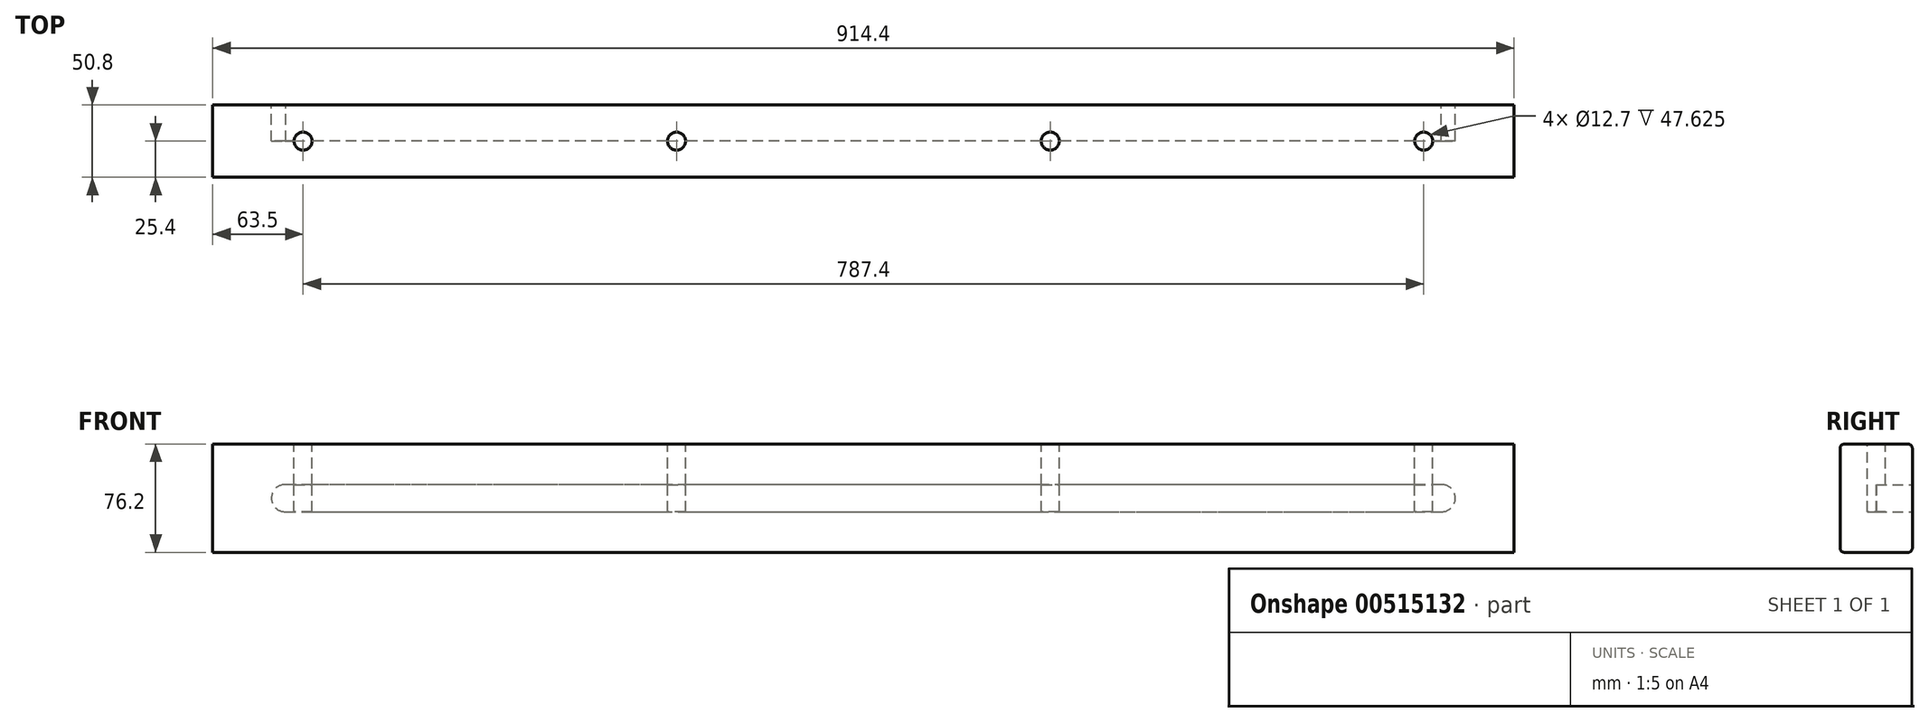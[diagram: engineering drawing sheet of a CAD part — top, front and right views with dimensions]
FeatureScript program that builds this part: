
annotation { "Feature Type Name" : "Feature", "Feature Type Description" : "" }
export const myFeature = defineFeature(function(context is Context, id is Id, definition is map)
    precondition{}
    {
        {
            var Q0;
            Q0=qCreatedBy(makeId("Front.planeOp"),FACE);
            var sketch = newSketch(context, id + "F0", { "sketchPlane" : qUnion([Q0])});
            skLineSegment(sketch, "E0.bottom", {"start": v(-457.2, 38.1) * mm, "end": v(457.2, 38.1) * mm});
            skLineSegment(sketch, "E0.top", {"start": v(-457.2, -38.1) * mm, "end": v(457.2, -38.1) * mm});
            skLineSegment(sketch, "E0.left", {"start": v(-457.2, 38.1) * mm, "end": v(-457.2, -38.1) * mm});
            skLineSegment(sketch, "E0.right", {"start": v(457.2, 38.1) * mm, "end": v(457.2, -38.1) * mm});
            skPoint(sketch, "E0.middle", {"position": v(0, 0) * mm});
            skSolve(sketch);
        }
        {
            var Q0;
            Q0 = qSketchRegion(id + "F0", true);
            extrude(context, id + "F1", {"entities" : qUnion([Q0]), "depth" : 50.8 * mm, "offsetDistance" : 25.4 * mm});
        }
        {
            var Q0;
            Q0=makeQuery(id+"F1.opExtrude","SWEPT_FACE",FACE,{"disambiguationData":[OSD([sQuery(id+"F0.wireOp",EDGE,"E0.bottom")])]});
            var sketch = newSketch(context, id + "F2", { "sketchPlane" : qUnion([Q0])});
            skLineSegment(sketch, "E1", {"start": v(-457.2, -25.4) * mm, "end": v(457.2, -25.4) * mm, "construction": true});
            skCircle(sketch, "E2", {"center": v(-393.7, -25.4) * mm, "radius": 6.35 * mm});
            skCircle(sketch, "E3", {"center": v(393.7, -25.4) * mm, "radius": 6.35 * mm});
            skCircle(sketch, "E4", {"center": v(-131.32, -25.4) * mm, "radius": 6.35 * mm});
            skCircle(sketch, "E5", {"center": v(131.32, -25.4) * mm, "radius": 6.35 * mm});
            skSolve(sketch);
        }
        {
            var Q0;
            Q0 = qSketchRegion(id + "F2", true);
            extrude(context, id + "F3", {"entities" : qUnion([Q0]), "operationType" : NewBodyOperationType.REMOVE, "oppositeDirection" : true, "depth" : 47.62 * mm, "offsetDistance" : 25.4 * mm});
        }
        {
            var Q0;
            Q0=makeQuery(id+"F1.opExtrude","CAP_FACE",FACE,{"disambiguationData":[OSD([sQuery(id+"F0.wireOp",EDGE,"E0.bottom"),sQuery(id+"F0.wireOp",EDGE,"E0.top"),sQuery(id+"F0.wireOp",EDGE,"E0.left"),sQuery(id+"F0.wireOp",EDGE,"E0.right")])],"isStart":true});
            var sketch = newSketch(context, id + "F4", { "sketchPlane" : qUnion([Q0])});
            skArc(sketch, "E6", {"start": v(-406.4, 9.53) * mm, "mid": v(-415.92, -0.23) * mm, "end": v(-405.93, -9.51) * mm});
            skLineSegment(sketch, "E7", {"start": v(-406.4, 9.53) * mm, "end": v(405.93, 9.52) * mm});
            skLineSegment(sketch, "E8", {"start": v(406.4, -9.51) * mm, "end": v(-405.93, -9.51) * mm});
            skArc(sketch, "E9", {"start": v(406.4, -9.51) * mm, "mid": v(415.92, 0.25) * mm, "end": v(405.93, 9.52) * mm});
            skSolve(sketch);
        }
        {
            var Q0;
            Q0 = qSketchRegion(id + "F4", true);
            extrude(context, id + "F5", {"entities" : qUnion([Q0]), "operationType" : NewBodyOperationType.REMOVE, "oppositeDirection" : true, "depth" : 25.4 * mm, "offsetDistance" : 25.4 * mm});
        }
        {
            var Q0;
            Q0=makeQuery(id+"F1.opExtrude","SWEPT_FACE",FACE,{"disambiguationData":[OSD([sQuery(id+"F0.wireOp",EDGE,"E0.left")])]});
            var sketch = newSketch(context, id + "F6", { "sketchPlane" : qUnion([Q0])});
            skPoint(sketch, "E10.middle", {"position": v(25.4, 0) * mm});
            skPoint(sketch, "E10.middle.positionSnap0", {"position": v(0, 0) * mm});
            skPoint(sketch, "E10.middle.positionSnap1", {"position": v(25.4, 38.1) * mm});
            skPoint(sketch, "E10.centerSnap0", {"position": v(0, 0) * mm});
            skPoint(sketch, "E10.centerSnap1", {"position": v(25.4, 38.1) * mm});
            skPoint(sketch, "E11.visualSharp", {"position": v(0, 38.1) * mm});
            skArc(sketch, "E11.filletArc", {"start": v(3.18, 38.1) * mm, "mid": v(0.93, 37.17) * mm, "end": v(0, 34.92) * mm});
            skPoint(sketch, "E12.visualSharp", {"position": v(50.8, 38.1) * mm});
            skArc(sketch, "E12.filletArc", {"start": v(50.8, 34.92) * mm, "mid": v(49.87, 37.17) * mm, "end": v(47.63, 38.1) * mm});
            skPoint(sketch, "E13.visualSharp", {"position": v(0, -38.1) * mm});
            skArc(sketch, "E13.filletArc", {"start": v(0, -34.93) * mm, "mid": v(0.93, -37.17) * mm, "end": v(3.18, -38.1) * mm});
            skPoint(sketch, "E14.visualSharp", {"position": v(50.8, -38.1) * mm});
            skArc(sketch, "E14.filletArc", {"start": v(47.63, -38.1) * mm, "mid": v(49.87, -37.17) * mm, "end": v(50.8, -34.93) * mm});
            skLineSegment(sketch, "E15.bottom", {"start": v(50.8, 38.1) * mm, "end": v(47.63, 38.1) * mm});
            skLineSegment(sketch, "E15.top", {"start": v(50.8, -38.1) * mm, "end": v(47.63, -38.1) * mm});
            skLineSegment(sketch, "E15.left", {"start": v(50.8, 38.1) * mm, "end": v(50.8, 34.92) * mm});
            skLineSegment(sketch, "E15.right", {"start": v(0, 38.1) * mm, "end": v(0, 34.92) * mm});
            skLineSegment(sketch, "E16.trimOffspring", {"start": v(3.18, 38.1) * mm, "end": v(0, 38.1) * mm});
            skLineSegment(sketch, "E17.trimOffspring", {"start": v(50.8, -34.93) * mm, "end": v(50.8, -38.1) * mm});
            skLineSegment(sketch, "E18.trimOffspring", {"start": v(0, -34.93) * mm, "end": v(0, -38.1) * mm});
            skLineSegment(sketch, "E19.trimOffspring", {"start": v(3.18, -38.1) * mm, "end": v(0, -38.1) * mm});
            skSolve(sketch);
        }
        {
            var Q0;
            Q0 = qSketchRegion(id + "F6", true);
            extrude(context, id + "F7", {"entities" : qUnion([Q0]), "operationType" : NewBodyOperationType.REMOVE, "endBound" : BoundingType.THROUGH_ALL, "oppositeDirection" : true, "depth" : 25.4 * mm, "offsetDistance" : 25.4 * mm});
        }
    });
